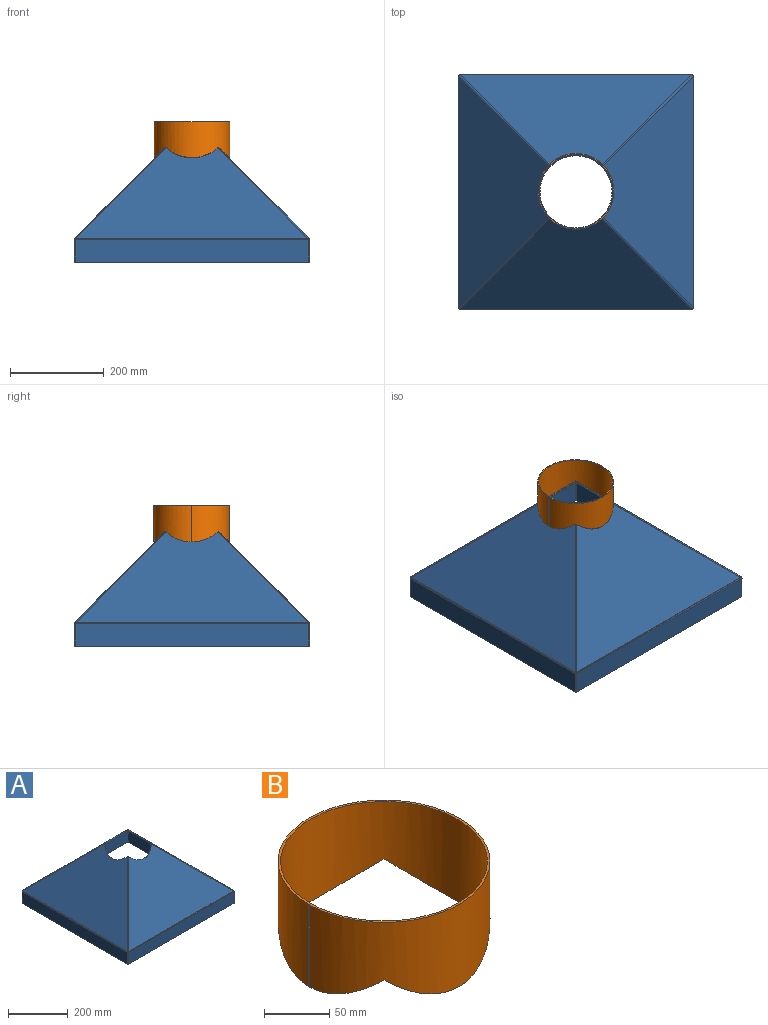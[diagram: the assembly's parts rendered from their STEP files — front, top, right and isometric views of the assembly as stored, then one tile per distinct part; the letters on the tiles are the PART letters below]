
ASSEMBLY  parts=2 mates=1
PART A: 68 faces, bbox 504x504x246.1 mm
  f0: plane 2.28x2mm, normal (0,0,1), area 4.6mm2, adj f3,f4,f5,f65
  f1: plane 48.22x2mm, normal (-1,0,0), area 96.4mm2, adj f2,f4,f5,f64
  f2: plane 499.96x2mm, normal (0,0,-1), area 999.9mm2, adj f1,f3,f4,f5
  f3: plane 48.22x2mm, normal (1,0,0), area 96.4mm2, adj f0,f2,f4,f5
  f4: plane 499.96x48.22mm, normal (0,-1,0), area 24107.5mm2, adj f0,f1,f2,f3,f66
  f5: plane 499.96x48.22mm, normal (0,1,0), area 24107.5mm2, adj f0,f1,f2,f3,f67
  f6: plane 2.28x2mm, normal (0,0,1), area 4.6mm2, adj f9,f11,f12,f61
  f7: plane 48.22x2mm, normal (1,0,0), area 96.4mm2, adj f8,f10,f11,f12
  f8: plane 499.96x2mm, normal (0,0,-1), area 999.9mm2, adj f7,f9,f11,f12
  f9: plane 48.22x2mm, normal (-1,0,0), area 96.4mm2, adj f6,f8,f11,f12
  f10: plane 2.28x2mm, normal (0,0,1), area 4.6mm2, adj f7,f11,f12,f60
  f11: plane 499.96x48.22mm, normal (0,1,0), area 24107.5mm2, adj f6,f7,f8,f9,f10,f62
  f12: plane 499.96x48.22mm, normal (0,-1,0), area 24107.5mm2, adj f6,f7,f8,f9,f10,f63
  f13: plane 2.28x2mm, normal (0,0,1), area 4.6mm2, adj f16,f18,f19,f41
  f14: plane 48.22x2mm, normal (0,-1,0), area 96.4mm2, adj f15,f17,f18,f19
  f15: plane 499.96x2mm, normal (0,0,-1), area 999.9mm2, adj f14,f16,f18,f19
  f16: plane 48.22x2mm, normal (0,1,0), area 96.4mm2, adj f13,f15,f18,f19
  f17: plane 2.28x2mm, normal (0,0,1), area 4.6mm2, adj f14,f18,f19,f40
  f18: plane 499.96x48.22mm, normal (1,0,0), area 24107.5mm2, adj f13,f14,f15,f16,f17,f42
  f19: plane 499.96x48.22mm, normal (-1,0,0), area 24107.5mm2, adj f13,f14,f15,f16,f17,f43
  f20: plane 48.22x2mm, normal (0,1,0), area 96.4mm2, adj f21,f23,f24,f25
  f21: plane 499.96x2mm, normal (0,0,-1), area 999.9mm2, adj f20,f22,f24,f25
  f22: plane 48.22x2mm, normal (0,-1,0), area 96.4mm2, adj f21,f24,f25,f53
  f23: plane 2.28x2mm, normal (0,0,1), area 4.6mm2, adj f20,f24,f25,f52
  f24: plane 499.96x48.22mm, normal (-1,0,0), area 24107.5mm2, adj f20,f21,f22,f23,f54
  f25: plane 499.96x48.22mm, normal (1,0,0), area 24107.5mm2, adj f20,f21,f22,f23,f55
  f26: plane 196.29x196.29mm, normal (-0.82,0.41,0.41), area 675.1mm2, adj f27,f28,f29,f64
  f27: extruded ~108.07x23.96mm, area 259.6mm2, adj f26,f28,f29,f37
  f28: plane 497.01x194.87mm, normal (0,-0.71,0.71), area 80875.4mm2, adj f26,f27,f38,f66
  f29: plane 497.01x194.87mm, normal (0,0.71,-0.71), area 80875.4mm2, adj f26,f27,f39,f67
  f30: extruded ~107.26x23.16mm, area 256.8mm2, adj f31,f32,f45,f56
  f31: plane 495.4x194.07mm, normal (0,0.71,0.71), area 80432.6mm2, adj f30,f46,f58,f62
  f32: plane 495.4x194.07mm, normal (0,-0.71,-0.71), area 80432.6mm2, adj f30,f47,f59,f63
  f33: extruded ~107.26x23.16mm, area 256.8mm2, adj f34,f35,f37,f45
  f34: plane 495.4x194.07mm, normal (0.71,0,0.71), area 80432.6mm2, adj f33,f38,f42,f46
  f35: plane 495.4x194.07mm, normal (-0.71,0,-0.71), area 80432.6mm2, adj f33,f39,f43,f47
  f36: plane 3.04x3.04mm, normal (0.58,-0.58,-0.58), area 6.9mm2, adj f38,f39,f40,f65
  f37: plane 3.04x3.04mm, normal (-0.58,0.58,0.58), area 6.9mm2, adj f27,f33,f38,f39
  f38: cylinder r=4.3mm len=197.11mm, axis (0.58,-0.58,-0.58), area 1513.6mm2, adj f28,f34,f36,f37
  f39: cylinder r=2.3mm len=195.7mm, axis (0.58,-0.58,-0.58), area 809.6mm2, adj f29,f35,f36,f37
  f40: plane 3.04x2.67mm, normal (0,-1,0), area 5.2mm2, adj f17,f36,f42,f43
  f41: plane 3.04x2.67mm, normal (0,1,0), area 5.2mm2, adj f13,f42,f43,f44
  f42: cylinder r=4.3mm len=495.4mm, axis (0,-1,0), area 1673.1mm2, adj f18,f34,f40,f41
  f43: cylinder r=2.3mm len=495.4mm, axis (0,-1,0), area 894.9mm2, adj f19,f35,f40,f41
  f44: plane 3.04x3.04mm, normal (0.58,0.58,-0.58), area 6.9mm2, adj f41,f46,f47,f60
  f45: plane 3.04x3.04mm, normal (-0.58,-0.58,0.58), area 6.9mm2, adj f30,f33,f46,f47
  f46: cylinder r=4.3mm len=197.11mm, axis (0.58,0.58,-0.58), area 1513.6mm2, adj f31,f34,f44,f45
  f47: cylinder r=2.3mm len=195.7mm, axis (0.58,0.58,-0.58), area 809.6mm2, adj f32,f35,f44,f45
  f48: plane 196.29x196.29mm, normal (0.41,-0.82,0.41), area 675.1mm2, adj f49,f50,f51,f53
  f49: extruded ~108.07x23.96mm, area 259.6mm2, adj f48,f50,f51,f56
  f50: plane 497.01x194.87mm, normal (-0.71,0,0.71), area 80875.4mm2, adj f48,f49,f54,f58
  f51: plane 497.01x194.87mm, normal (0.71,0,-0.71), area 80875.4mm2, adj f48,f49,f55,f59
  f52: plane 3.04x2.67mm, normal (0,1,0), area 5.2mm2, adj f23,f54,f55,f57
  f53: bspline ~3.04x2.67mm, area 5.4mm2, adj f22,f48,f54,f55
  f54: cylinder r=4.3mm len=497.68mm, axis (0,1,0), area 1679.6mm2, adj f24,f50,f52,f53
  f55: cylinder r=2.3mm len=497.68mm, axis (0,1,0), area 898.4mm2, adj f25,f51,f52,f53
  f56: plane 3.04x3.04mm, normal (0.58,-0.58,0.58), area 6.9mm2, adj f30,f49,f58,f59
  f57: plane 3.04x3.04mm, normal (-0.58,0.58,-0.58), area 6.9mm2, adj f52,f58,f59,f61
  f58: cylinder r=4.3mm len=197.11mm, axis (0.58,-0.58,0.58), area 1513.6mm2, adj f31,f50,f56,f57
  f59: cylinder r=2.3mm len=195.7mm, axis (0.58,-0.58,0.58), area 809.6mm2, adj f32,f51,f56,f57
  f60: plane 3.04x2.67mm, normal (1,0,0), area 5.2mm2, adj f10,f44,f62,f63
  f61: plane 3.04x2.67mm, normal (-1,0,0), area 5.2mm2, adj f6,f57,f62,f63
  f62: cylinder r=4.3mm len=495.4mm, axis (1,0,0), area 1673.1mm2, adj f11,f31,f60,f61
  f63: cylinder r=2.3mm len=495.4mm, axis (1,0,0), area 894.9mm2, adj f12,f32,f60,f61
  f64: bspline ~3.04x2.67mm, area 5.4mm2, adj f1,f26,f66,f67
  f65: plane 3.04x2.67mm, normal (1,0,0), area 5.2mm2, adj f0,f36,f66,f67
  f66: cylinder r=4.3mm len=497.68mm, axis (-1,0,0), area 1679.6mm2, adj f4,f28,f64,f65
  f67: cylinder r=2.3mm len=497.68mm, axis (-1,0,0), area 898.4mm2, adj f5,f29,f64,f65
PART B: 10 faces, bbox 162x324x158.1 mm
  f0: plane 162x162mm, normal (0,0,1), area 1002.5mm2, adj f1,f7,f8,f9
  f1: plane 77x2mm, normal (-0.01,1,0), area 154mm2, adj f0,f2,f8,f9
  f2: bspline ~162x162mm, area 134.7mm2, adj f1,f3,f8,f9
  f3: bspline ~114.55x25.07mm, area 272.3mm2, adj f2,f4,f8,f9
  f4: bspline ~114.55x25.07mm, area 272.3mm2, adj f3,f5,f8,f9
  f5: bspline ~114.55x25.07mm, area 272.3mm2, adj f4,f6,f8,f9
  f6: bspline ~162x162mm, area 134.7mm2, adj f5,f7,f8,f9
  f7: plane 77x2mm, normal (-0.01,-1,0), area 154mm2, adj f0,f6,f8,f9
  f8: cylinder r=81mm len=162mm, axis (0,0,-1), area 35071.5mm2, adj f0,f1,f2,f3,f4,f5,f6,f7
  f9: cylinder r=79mm len=158mm, axis (0,0,-1), area 34205.5mm2, adj f0,f1,f2,f3,f4,f5,f6,f7
PLACE A rot(axis=(0.4,-0.26,0.88),0deg) t=(-236.1,-660.85,573.9)mm
PLACE B rot(axis=(0.4,-0.26,0.88),0deg) t=(-236.33,-659.85,573.9)mm
MATE parallel B.f0 <-> A.f2  axis (0,0,1) through (-236.1,-659.85,873.9)mm
